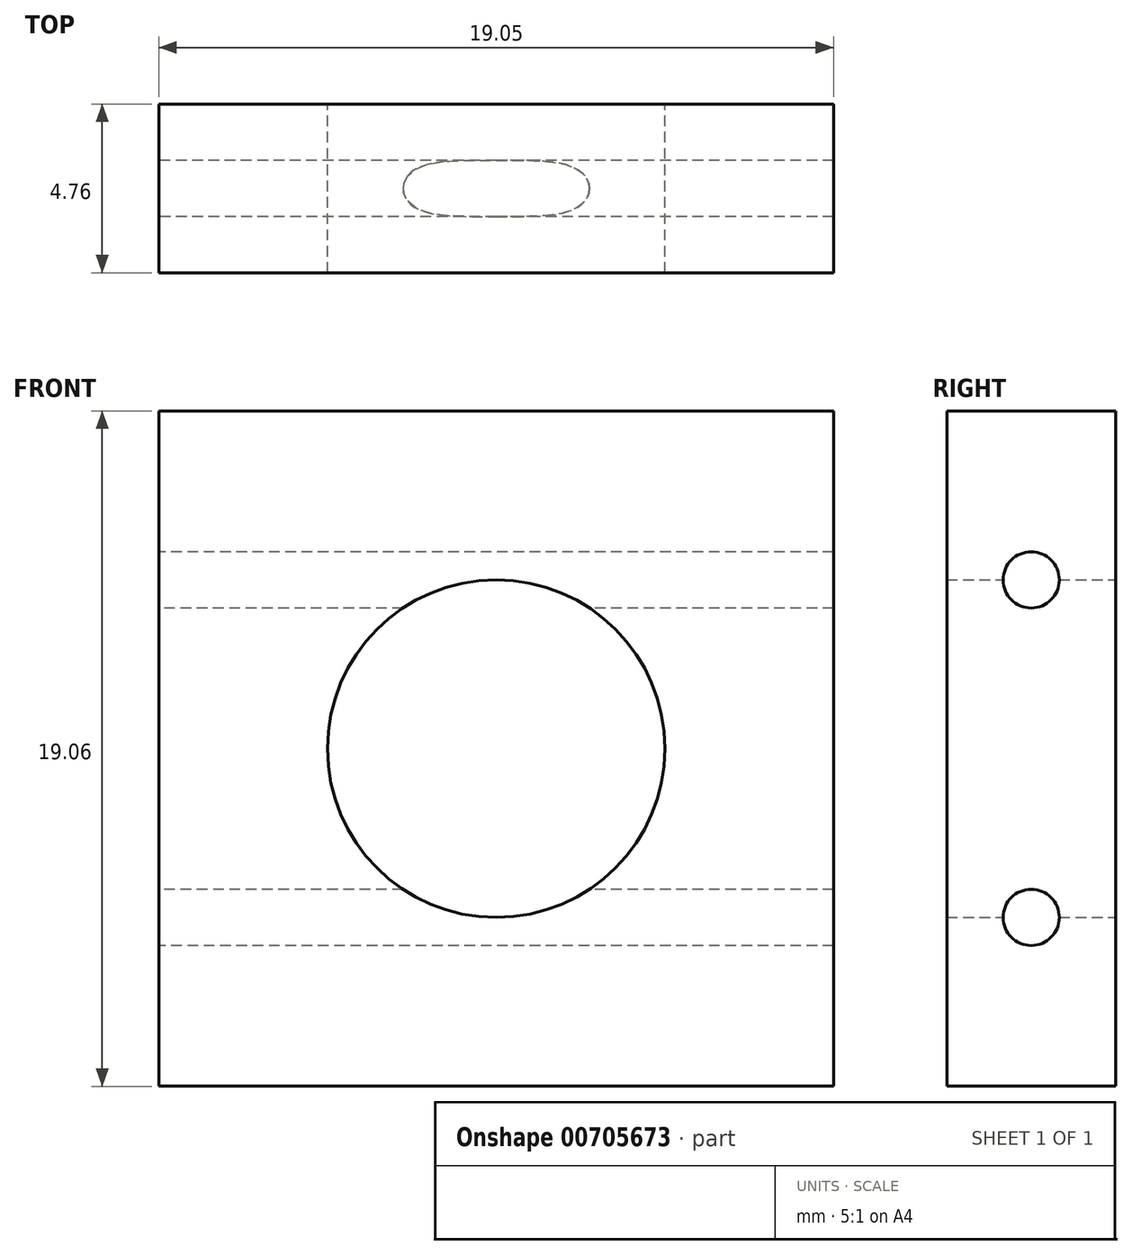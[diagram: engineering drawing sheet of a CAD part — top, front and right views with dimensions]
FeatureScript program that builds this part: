
annotation { "Feature Type Name" : "Feature", "Feature Type Description" : "" }
export const myFeature = defineFeature(function(context is Context, id is Id, definition is map)
    precondition{}
    {
        {
            var Q0;
            Q0=qCreatedBy(makeId("Right.planeOp"),FACE);
            var sketch = newSketch(context, id + "F0", { "sketchPlane" : qUnion([Q0])});
            skLineSegment(sketch, "E0.bottom", {"start": v(-2.38, 9.53) * mm, "end": v(2.38, 9.53) * mm});
            skLineSegment(sketch, "E0.top", {"start": v(-2.38, -9.53) * mm, "end": v(2.38, -9.53) * mm});
            skLineSegment(sketch, "E0.left", {"start": v(-2.38, 9.53) * mm, "end": v(-2.38, -9.53) * mm});
            skLineSegment(sketch, "E0.right", {"start": v(2.38, 9.53) * mm, "end": v(2.38, -9.53) * mm});
            skPoint(sketch, "E0.middle", {"position": v(0, 0) * mm});
            skLineSegment(sketch, "E1", {"start": v(0, 4.76) * mm, "end": v(0, -4.76) * mm, "construction": true});
            skCircle(sketch, "E2", {"center": v(0, 4.76) * mm, "radius": 0.8 * mm});
            skCircle(sketch, "E3", {"center": v(0, -4.76) * mm, "radius": 0.8 * mm});
            skSolve(sketch);
        }
        {
            var Q0;
            Q0=makeQuery(id+"F0.imprint","IMPRINT",FACE,{"disambiguationData":[TD([[makeQuery(id+"F0.imprint","IMPRINT",EDGE,{"derivedFrom":sQuery(id+"F0.wireOp",EDGE,"E0.bottom")}),-1.0]])]});
            extrude(context, id + "F1", {"entities" : qUnion([Q0]), "depth" : 19.05 * mm, "offsetDistance" : 25.4 * mm});
        }
        {
            var Q0;
            Q0=makeQuery(id+"F1.opExtrude","SWEPT_FACE",FACE,{"disambiguationData":[OSD([sQuery(id+"F0.wireOp",EDGE,"E0.right")])]});
            var sketch = newSketch(context, id + "F2", { "sketchPlane" : qUnion([Q0])});
            skCircle(sketch, "E4", {"center": v(-9.53, 0) * mm, "radius": 4.76 * mm});
            skPoint(sketch, "E4.centerSnap0", {"position": v(-9.53, 9.53) * mm});
            skSolve(sketch);
        }
        {
            var Q0;
            Q0=makeQuery(id+"F2.imprint","IMPRINT",FACE,{"disambiguationData":[TD([[makeQuery(id+"F2.imprint","IMPRINT",EDGE,{"derivedFrom":sQuery(id+"F2.wireOp",EDGE,"E4")}),1.0]])]});
            extrude(context, id + "F3", {"entities" : qUnion([Q0]), "operationType" : NewBodyOperationType.REMOVE, "oppositeDirection" : true, "depth" : 25.4 * mm, "offsetDistance" : 25.4 * mm});
        }
    });
